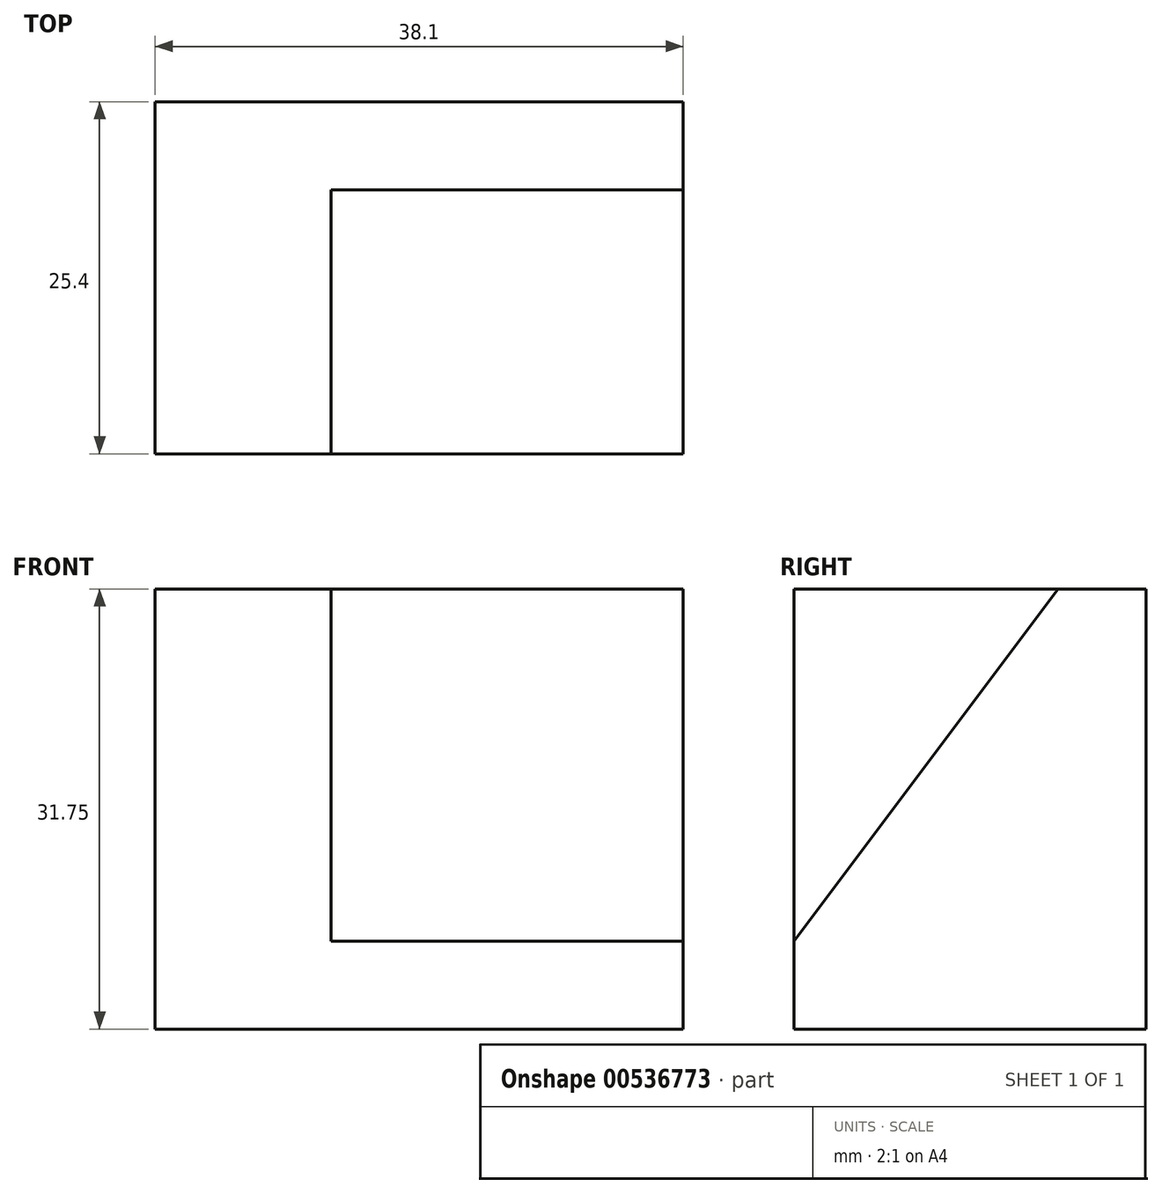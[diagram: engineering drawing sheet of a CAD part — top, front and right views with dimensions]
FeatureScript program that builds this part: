
annotation { "Feature Type Name" : "Feature", "Feature Type Description" : "" }
export const myFeature = defineFeature(function(context is Context, id is Id, definition is map)
    precondition{}
    {
        {
            var Q0;
            Q0=qCreatedBy(makeId("Front.planeOp"),FACE);
            var sketch = newSketch(context, id + "F0", { "sketchPlane" : qUnion([Q0])});
            skLineSegment(sketch, "E0", {"start": v(-35.97, 31.75) * mm, "end": v(-35.97, 0) * mm});
            skLineSegment(sketch, "E1", {"start": v(-35.97, 0) * mm, "end": v(2.13, 0) * mm});
            skLineSegment(sketch, "E2", {"start": v(2.13, 0) * mm, "end": v(2.13, 31.75) * mm});
            skLineSegment(sketch, "E3", {"start": v(2.13, 31.75) * mm, "end": v(-35.97, 31.75) * mm});
            skSolve(sketch);
        }
        {
            var Q0;
            Q0=makeQuery(id+"F0.imprint","IMPRINT",FACE,{"disambiguationData":[TD([[makeQuery(id+"F0.imprint","IMPRINT",EDGE,{"derivedFrom":sQuery(id+"F0.wireOp",EDGE,"E0")}),1.0]])]});
            extrude(context, id + "F1", {"entities" : qUnion([Q0]), "depth" : 25.4 * mm, "offsetDistance" : 25.4 * mm});
        }
        {
            var Q0;
            Q0=makeQuery(id+"F1.opExtrude","SWEPT_FACE",FACE,{"disambiguationData":[OSD([sQuery(id+"F0.wireOp",EDGE,"E2")])]});
            var sketch = newSketch(context, id + "F2", { "sketchPlane" : qUnion([Q0])});
            skLineSegment(sketch, "E4", {"start": v(-6.35, 31.75) * mm, "end": v(-25.4, 6.35) * mm});
            skLineSegment(sketch, "E5", {"start": v(-6.35, 31.75) * mm, "end": v(0, 31.75) * mm});
            skLineSegment(sketch, "E6", {"start": v(-25.4, 6.35) * mm, "end": v(-25.4, 0) * mm});
            skSolve(sketch);
        }
        {
            var Q0;
            {var subQ0=sQuery(id+"F2.wireOp",EDGE,"E4");Q0=makeQuery(id+"F2.imprint","IMPRINT",FACE,{"disambiguationData":[TD([[makeQuery(id+"F2.imprint","IMPRINT",EDGE,{"derivedFrom":subQ0}),-1.0]])]});}
            extrude(context, id + "F3", {"entities" : qUnion([Q0]), "operationType" : NewBodyOperationType.REMOVE, "oppositeDirection" : true, "depth" : 25.4 * mm, "offsetDistance" : 25.4 * mm});
        }
    });
